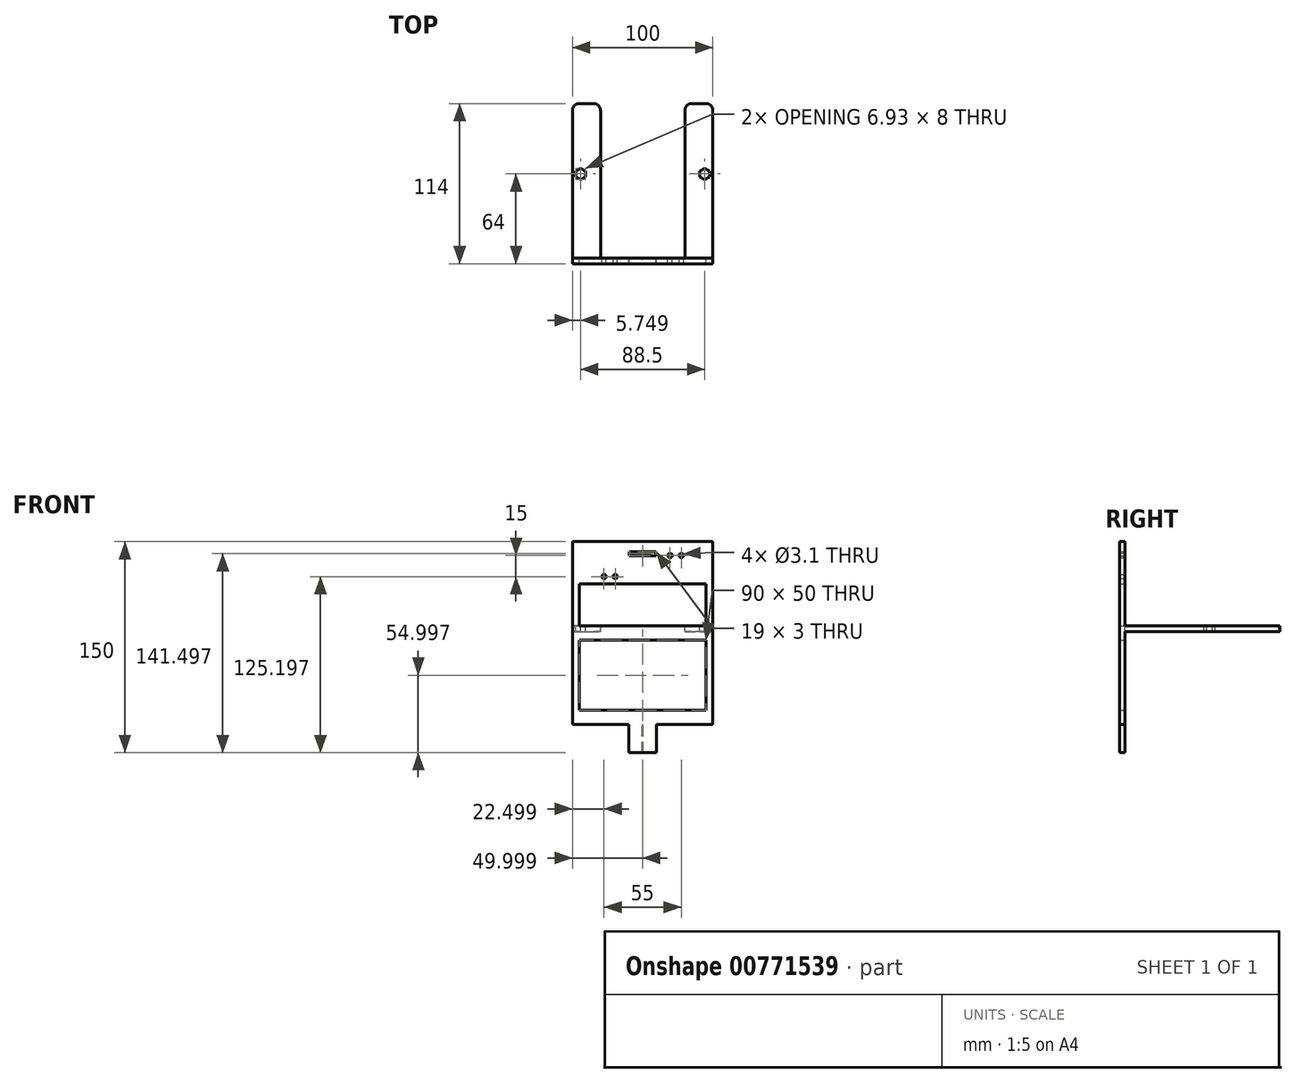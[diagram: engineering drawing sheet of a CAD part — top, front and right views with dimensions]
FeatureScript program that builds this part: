
annotation { "Feature Type Name" : "Feature", "Feature Type Description" : "" }
export const myFeature = defineFeature(function(context is Context, id is Id, definition is map)
    precondition{}
    {
        {
            var Q0;
            Q0=qCreatedBy(makeId("Front.planeOp"),FACE);
            var sketch = newSketch(context, id + "F0", { "sketchPlane" : qUnion([Q0])});
            skLineSegment(sketch, "E0.bottom", {"start": v(-49.14, 66.16) * mm, "end": v(50.86, 66.16) * mm});
            skLineSegment(sketch, "E0.top", {"start": v(-49.14, -83.84) * mm, "end": v(50.86, -83.84) * mm});
            skLineSegment(sketch, "E0.left", {"start": v(-49.14, 66.16) * mm, "end": v(-49.14, -83.84) * mm});
            skLineSegment(sketch, "E0.right", {"start": v(50.86, 66.16) * mm, "end": v(50.86, -83.84) * mm});
            skLineSegment(sketch, "E1.bottom", {"start": v(50.86, -83.84) * mm, "end": v(10.86, -83.84) * mm});
            skLineSegment(sketch, "E1.top", {"start": v(50.86, -63.84) * mm, "end": v(10.86, -63.84) * mm});
            skLineSegment(sketch, "E1.left", {"start": v(50.86, -83.84) * mm, "end": v(50.86, -63.84) * mm});
            skLineSegment(sketch, "E1.right", {"start": v(10.86, -83.84) * mm, "end": v(10.86, -63.84) * mm});
            skLineSegment(sketch, "E2.bottom", {"start": v(-49.14, -83.84) * mm, "end": v(-9.14, -83.84) * mm});
            skLineSegment(sketch, "E2.top", {"start": v(-49.14, -63.84) * mm, "end": v(-9.14, -63.84) * mm});
            skLineSegment(sketch, "E2.left", {"start": v(-49.14, -83.84) * mm, "end": v(-49.14, -63.84) * mm});
            skLineSegment(sketch, "E2.right", {"start": v(-9.14, -83.84) * mm, "end": v(-9.14, -63.84) * mm});
            skLineSegment(sketch, "E3.bottom", {"start": v(-44.14, -3.84) * mm, "end": v(45.86, -3.84) * mm});
            skLineSegment(sketch, "E3.top", {"start": v(-44.14, -53.84) * mm, "end": v(45.86, -53.84) * mm});
            skLineSegment(sketch, "E3.left", {"start": v(-44.14, -3.84) * mm, "end": v(-44.14, -53.84) * mm});
            skLineSegment(sketch, "E3.right", {"start": v(45.86, -3.84) * mm, "end": v(45.86, -53.84) * mm});
            skLineSegment(sketch, "E4.bottom", {"start": v(-44.14, 36.16) * mm, "end": v(45.86, 36.16) * mm});
            skLineSegment(sketch, "E4.top", {"start": v(-44.14, 6.16) * mm, "end": v(45.86, 6.16) * mm});
            skLineSegment(sketch, "E4.left", {"start": v(-44.14, 36.16) * mm, "end": v(-44.14, 6.16) * mm});
            skLineSegment(sketch, "E4.right", {"start": v(45.86, 36.16) * mm, "end": v(45.86, 6.16) * mm});
            skLineSegment(sketch, "E5.bottom", {"start": v(10.36, 56.16) * mm, "end": v(-8.64, 56.16) * mm});
            skLineSegment(sketch, "E5.top", {"start": v(10.36, 59.16) * mm, "end": v(-8.64, 59.16) * mm});
            skLineSegment(sketch, "E5.left", {"start": v(10.36, 56.16) * mm, "end": v(10.36, 59.16) * mm});
            skLineSegment(sketch, "E5.right", {"start": v(-8.64, 56.16) * mm, "end": v(-8.64, 59.16) * mm});
            skCircle(sketch, "E6", {"center": v(28.36, 56.36) * mm, "radius": 1.55 * mm});
            skCircle(sketch, "E7", {"center": v(-26.64, 41.36) * mm, "radius": 1.55 * mm});
            skCircle(sketch, "E8", {"center": v(20.36, 56.36) * mm, "radius": 1.55 * mm});
            skCircle(sketch, "E9", {"center": v(-18.64, 41.36) * mm, "radius": 1.55 * mm});
            skSolve(sketch);
        }
        {
            var Q0;
            Q0=makeQuery(id+"F0.imprint","IMPRINT",FACE,{"disambiguationData":[TD([[makeQuery(id+"F0.imprint","IMPRINT",EDGE,{"derivedFrom":sQuery(id+"F0.wireOp",EDGE,"E0.bottom")}),-1.0]])]});
            extrude(context, id + "F1", {"entities" : qUnion([Q0]), "depth" : 4 * mm, "offsetDistance" : 25 * mm});
        }
        {
            var Q0;
            Q0=makeQuery(id+"F1.opExtrude","SWEPT_FACE",FACE,{"disambiguationData":[OSD([sQuery(id+"F0.wireOp",EDGE,"E4.top")])]});
            var sketch = newSketch(context, id + "F2", { "sketchPlane" : qUnion([Q0])});
            skLineSegment(sketch, "E10.0", {"start": v(-49.14, 0) * mm, "end": v(50.86, 0) * mm});
            skLineSegment(sketch, "E11.bottom", {"start": v(-49.14, 0) * mm, "end": v(-29.14, 0) * mm});
            skLineSegment(sketch, "E11.top", {"start": v(-44.14, 110) * mm, "end": v(-34.14, 110) * mm});
            skLineSegment(sketch, "E11.left", {"start": v(-49.14, 0) * mm, "end": v(-49.14, 105) * mm});
            skLineSegment(sketch, "E11.right", {"start": v(-29.14, 0) * mm, "end": v(-29.14, 105) * mm});
            skLineSegment(sketch, "E12.bottom", {"start": v(45.86, 110) * mm, "end": v(35.86, 110) * mm});
            skLineSegment(sketch, "E12.top", {"start": v(50.86, 0) * mm, "end": v(30.86, 0) * mm});
            skLineSegment(sketch, "E12.left", {"start": v(50.86, 105) * mm, "end": v(50.86, 0) * mm});
            skLineSegment(sketch, "E12.right", {"start": v(30.86, 105) * mm, "end": v(30.86, 0) * mm});
            skPoint(sketch, "E13.visualSharp", {"position": v(-49.14, 110) * mm});
            skArc(sketch, "E13.filletArc", {"start": v(-44.14, 110) * mm, "mid": v(-47.68, 108.54) * mm, "end": v(-49.14, 105) * mm});
            skPoint(sketch, "E14.visualSharp", {"position": v(-29.14, 110) * mm});
            skArc(sketch, "E14.filletArc", {"start": v(-29.14, 105) * mm, "mid": v(-30.6, 108.54) * mm, "end": v(-34.14, 110) * mm});
            skPoint(sketch, "E15.visualSharp", {"position": v(50.86, 110) * mm});
            skArc(sketch, "E15.filletArc", {"start": v(50.86, 105) * mm, "mid": v(49.4, 108.54) * mm, "end": v(45.86, 110) * mm});
            skPoint(sketch, "E16.visualSharp", {"position": v(30.86, 110) * mm});
            skArc(sketch, "E16.filletArc", {"start": v(35.86, 110) * mm, "mid": v(32.32, 108.54) * mm, "end": v(30.86, 105) * mm});
            skCircle(sketch, "E17.cCircle", {"center": v(-43.4, 60) * mm, "radius": 3.46 * mm, "construction": true});
            skLineSegment(sketch, "E17.0", {"start": v(-43.4, 64) * mm, "end": v(-39.93, 62) * mm});
            skLineSegment(sketch, "E17.1", {"start": v(-39.93, 62) * mm, "end": v(-39.93, 58) * mm});
            skLineSegment(sketch, "E17.2", {"start": v(-39.93, 58) * mm, "end": v(-43.4, 56) * mm});
            skLineSegment(sketch, "E17.3", {"start": v(-43.4, 56) * mm, "end": v(-46.85, 58) * mm});
            skLineSegment(sketch, "E17.4", {"start": v(-46.85, 58) * mm, "end": v(-46.85, 62) * mm});
            skLineSegment(sketch, "E17.5", {"start": v(-46.85, 62) * mm, "end": v(-43.4, 64) * mm});
            skPoint(sketch, "E17.0.midPoint", {"position": v(-41.66, 63) * mm});
            skLineSegment(sketch, "E18", {"start": v(0.86, -4) * mm, "end": v(0.86, 92.09) * mm, "construction": true});
            skCircle(sketch, "E19.MirrorC", {"center": v(45.1, 60) * mm, "radius": 3.46 * mm, "construction": true});
            skLineSegment(sketch, "E20.MirrorCS", {"start": v(48.57, 62) * mm, "end": v(45.1, 64) * mm});
            skLineSegment(sketch, "E21.MirrorCS", {"start": v(45.1, 64) * mm, "end": v(41.65, 62) * mm});
            skLineSegment(sketch, "E22.MirrorCS", {"start": v(41.65, 62) * mm, "end": v(41.65, 58) * mm});
            skLineSegment(sketch, "E23.MirrorCS", {"start": v(41.65, 58) * mm, "end": v(45.1, 56) * mm});
            skLineSegment(sketch, "E24.MirrorCS", {"start": v(45.1, 56) * mm, "end": v(48.57, 58) * mm});
            skLineSegment(sketch, "E25.MirrorCS", {"start": v(48.57, 58) * mm, "end": v(48.57, 62) * mm});
            skSolve(sketch);
        }
        {
            var Q0;
            Q0=qSketchRegion(id+"F2",true);
            extrude(context, id + "F3", {"entities" : qUnion([Q0]), "operationType" : NewBodyOperationType.ADD, "oppositeDirection" : true, "depth" : 4 * mm, "offsetDistance" : 25 * mm});
        }
        {
            var Q0;
            {var subQ0=sQuery(id+"F0.wireOp",EDGE,"E3.left");var subQ13=sQuery(id+"F0.wireOp",EDGE,"E3.top");var subQ14=sQuery(id+"F0.wireOp",EDGE,"E3.bottom");var subQ15=sQuery(id+"F0.wireOp",EDGE,"E2.right");var subQ17=sQuery(id+"F0.wireOp",EDGE,"E2.top");var subQ19=sQuery(id+"F0.wireOp",EDGE,"E1.right");var subQ20=sQuery(id+"F0.wireOp",EDGE,"E0.top");var subQ21=sQuery(id+"F0.wireOp",EDGE,"E0.left");var subQ22=sQuery(id+"F0.wireOp",EDGE,"E0.right");var subQ33=sQuery(id+"F0.wireOp",EDGE,"E1.top");var subQ34=sQuery(id+"F0.wireOp",EDGE,"E3.right");var subQ35=sQuery(id+"F0.wireOp",EDGE,"E4.top");Q0=makeQuery(id+"F3.boolean.opBoolean","SPLIT",FACE,{"disambiguationData":[TD([makeQuery(id+"F1.opExtrude","SWEPT_FACE",FACE,{"disambiguationData":[OSD([subQ20])]})])],"derivedFrom":makeQuery(id+"F1.opExtrude","CAP_FACE",FACE,{"disambiguationData":[OSD([sQuery(id+"F0.wireOp",EDGE,"E0.bottom"),subQ20,subQ21,subQ22,subQ33,subQ19,subQ17,subQ15,subQ14,subQ13,subQ0,subQ34,sQuery(id+"F0.wireOp",EDGE,"E4.bottom"),subQ35,sQuery(id+"F0.wireOp",EDGE,"E4.left"),sQuery(id+"F0.wireOp",EDGE,"E4.right"),sQuery(id+"F0.wireOp",EDGE,"E5.bottom"),sQuery(id+"F0.wireOp",EDGE,"E5.top"),sQuery(id+"F0.wireOp",EDGE,"E5.left"),sQuery(id+"F0.wireOp",EDGE,"E5.right"),sQuery(id+"F0.wireOp",EDGE,"E6"),sQuery(id+"F0.wireOp",EDGE,"E7")])],"isStart":true})});}
            var sketch = newSketch(context, id + "F4", { "sketchPlane" : qUnion([Q0])});
            skLineSegment(sketch, "E26.bottom", {"start": v(-1.1, -53.84) * mm, "end": v(-0.6, -53.84) * mm});
            skLineSegment(sketch, "E26.top", {"start": v(-1.1, -83.84) * mm, "end": v(-0.6, -83.84) * mm});
            skLineSegment(sketch, "E27.bottom", {"start": v(-0.6, -83.84) * mm, "end": v(-1.1, -83.84) * mm});
            skLineSegment(sketch, "E27.top", {"start": v(-0.6, -63.84) * mm, "end": v(-1.1, -63.84) * mm});
            skLineSegment(sketch, "E27.left", {"start": v(-0.6, -83.84) * mm, "end": v(-0.6, -63.84) * mm});
            skLineSegment(sketch, "E27.right", {"start": v(-1.1, -83.84) * mm, "end": v(-1.1, -63.84) * mm});
            skSolve(sketch);
        }
        {
            var Q0;
            Q0=qSketchRegion(id+"F4",true);
            extrude(context, id + "F5", {"entities" : qUnion([Q0]), "operationType" : NewBodyOperationType.REMOVE, "oppositeDirection" : true, "depth" : 0.5 * mm, "offsetDistance" : 25 * mm});
        }
    });
